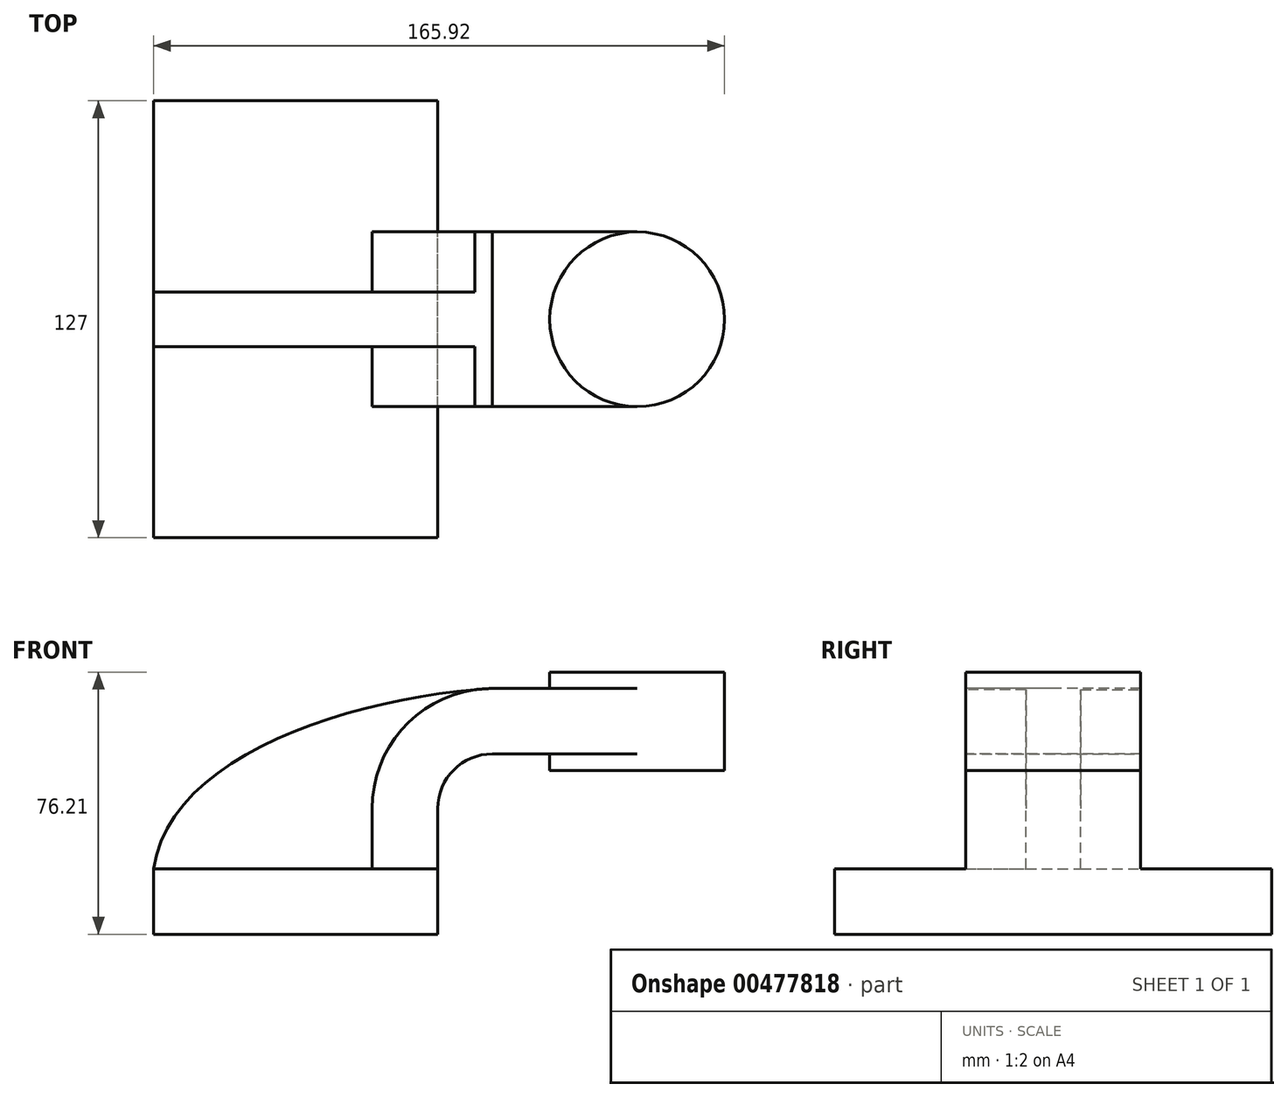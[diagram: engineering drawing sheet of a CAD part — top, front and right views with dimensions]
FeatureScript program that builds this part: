
annotation { "Feature Type Name" : "Feature", "Feature Type Description" : "" }
export const myFeature = defineFeature(function(context is Context, id is Id, definition is map)
    precondition{}
    {
        {
            var Q0;
            Q0=qCreatedBy(makeId("Front.planeOp"),FACE);
            var sketch = newSketch(context, id + "F0", { "sketchPlane" : qUnion([Q0])});
            skLineSegment(sketch, "E0.bottom", {"start": v(-41.28, 9.52) * mm, "end": v(41.27, 9.53) * mm});
            skLineSegment(sketch, "E0.top", {"start": v(-41.28, -9.53) * mm, "end": v(41.28, -9.53) * mm});
            skLineSegment(sketch, "E0.left", {"start": v(-41.28, 9.52) * mm, "end": v(-41.27, -9.53) * mm});
            skLineSegment(sketch, "E0.right", {"start": v(41.27, 9.53) * mm, "end": v(41.28, -9.52) * mm});
            skPoint(sketch, "E0.middle", {"position": v(0, 0) * mm});
            skLineSegment(sketch, "E1", {"start": v(41.27, 9.53) * mm, "end": v(41.27, 27) * mm});
            skArc(sketch, "E2", {"start": v(41.27, 27) * mm, "mid": v(45.92, 38.23) * mm, "end": v(57.15, 42.88) * mm});
            skLineSegment(sketch, "E3", {"start": v(57.15, 42.88) * mm, "end": v(99.24, 42.88) * mm});
            skLineSegment(sketch, "E4.0", {"start": v(57.15, 61.93) * mm, "end": v(99.24, 61.93) * mm});
            skArc(sketch, "E4.1", {"start": v(22.22, 27) * mm, "mid": v(32.45, 51.7) * mm, "end": v(57.15, 61.93) * mm});
            skLineSegment(sketch, "E4.2", {"start": v(22.22, 9.53) * mm, "end": v(22.22, 27) * mm});
            skLineSegment(sketch, "E5.bottom", {"start": v(124.64, 38.1) * mm, "end": v(73.84, 38.1) * mm});
            skLineSegment(sketch, "E5.top", {"start": v(124.64, 66.67) * mm, "end": v(73.84, 66.67) * mm});
            skLineSegment(sketch, "E5.left", {"start": v(124.64, 38.1) * mm, "end": v(124.64, 66.67) * mm});
            skLineSegment(sketch, "E5.right", {"start": v(73.84, 38.1) * mm, "end": v(73.84, 66.67) * mm});
            skPoint(sketch, "E5.middle", {"position": v(99.24, 52.39) * mm});
            skFitSpline(sketch, "E6", {"points": [v(-41.28, 9.52) * mm, v(57.15, 61.93) * mm], "startDerivative": vector(14.16, 99.56) * mm, "endDerivative": vector(120.5, 7.1) * mm});
            skLineSegment(sketch, "E7", {"start": v(99.24, 38.1) * mm, "end": v(99.24, 66.67) * mm});
            skSolve(sketch);
        }
        {
            var Q0;
            Q0=makeQuery(id+"F0.imprint","IMPRINT",FACE,{"disambiguationData":[TD([[makeQuery(id+"F0.imprint","IMPRINT",EDGE,{"derivedFrom":sQuery(id+"F0.wireOp",EDGE,"E0.top")}),1.0]])]});
            extrude(context, id + "F1", {"entities" : qUnion([Q0]), "endBound" : BoundingType.SYMMETRIC, "depth" : 127 * mm});
        }
        {
            var Q0;
            {var subQ3=sQuery(id+"F0.wireOp",EDGE,"E4.2");Q0=makeQuery(id+"F0.imprint","IMPRINT",FACE,{"disambiguationData":[TD([[makeQuery(id+"F0.imprint","IMPRINT",EDGE,{"derivedFrom":subQ3}),1.0]])]});}
            extrude(context, id + "F2", {"entities" : qUnion([Q0]), "operationType" : NewBodyOperationType.ADD, "endBound" : BoundingType.SYMMETRIC, "depth" : 15.88 * mm});
        }
        {
            var Q0;
            {var subQ4=sQuery(id+"F0.wireOp",EDGE,"E1");Q0=makeQuery(id+"F0.imprint","IMPRINT",FACE,{"disambiguationData":[TD([[makeQuery(id+"F0.imprint","IMPRINT",EDGE,{"derivedFrom":subQ4}),1.0]])]});}
            var Q1;
            {var subQ0=sQuery(id+"F0.wireOp",EDGE,"E7");var subQ1=sQuery(id+"F0.wireOp",EDGE,"E3");var subQ2=makeQuery(id+"F0.imprint","INTERSECT",VERTEX,{"derivedFrom":[subQ1,subQ0]});Q1=makeQuery(id+"F0.imprint","IMPRINT",FACE,{"disambiguationData":[TD([[makeQuery(id+"F0.imprint","IMPRINT",EDGE,{"disambiguationData":[TD([[subQ2,1.0]])],"derivedFrom":subQ1}),1.0]])]});}
            extrude(context, id + "F3", {"entities" : qUnion([Q0, Q1]), "operationType" : NewBodyOperationType.ADD, "endBound" : BoundingType.SYMMETRIC, "depth" : 50.8 * mm});
        }
        {
            var Q0;
            {var subQ0=sQuery(id+"F0.wireOp",EDGE,"E5.left");Q0=makeQuery(id+"F0.imprint","IMPRINT",FACE,{"disambiguationData":[TD([[makeQuery(id+"F0.imprint","IMPRINT",EDGE,{"derivedFrom":subQ0}),1.0]])]});}
            var Q1;
            Q1=sQuery(id+"F0.wireOp",EDGE,"E7");
            revolve(context, id + "F4", {"operationType" : NewBodyOperationType.ADD, "entities" : qUnion([Q0]), "axis" : qUnion([Q1]), "revolveType" : RevolveType.FULL});
        }
    });
